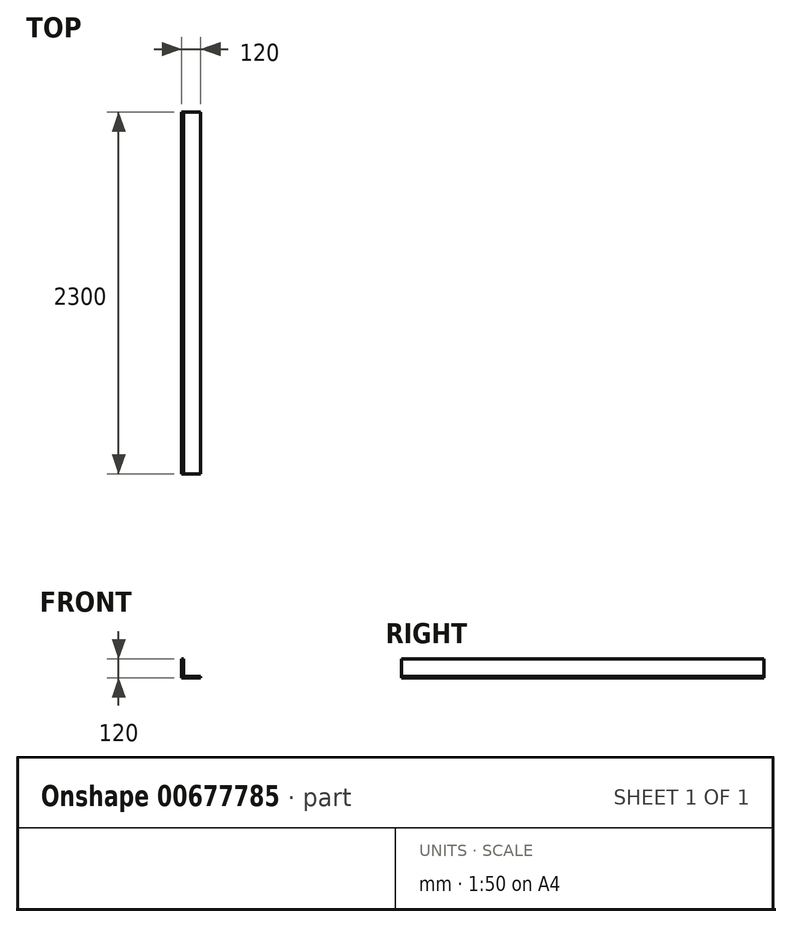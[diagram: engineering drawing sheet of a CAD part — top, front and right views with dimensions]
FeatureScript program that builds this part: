
annotation { "Feature Type Name" : "Feature", "Feature Type Description" : "" }
export const myFeature = defineFeature(function(context is Context, id is Id, definition is map)
    precondition{}
    {
        {
            var Q0;
            Q0=qCreatedBy(makeId("Front.planeOp"),FACE);
            var sketch = newSketch(context, id + "F0", { "sketchPlane" : qUnion([Q0])});
            skLineSegment(sketch, "E0.bottom", {"start": v(-43.33, -43.33) * mm, "end": v(76.67, -43.33) * mm});
            skLineSegment(sketch, "E0.top", {"start": v(-43.33, 76.67) * mm, "end": v(-33.33, 76.67) * mm});
            skLineSegment(sketch, "E0.left", {"start": v(-43.33, -43.33) * mm, "end": v(-43.33, 76.67) * mm});
            skLineSegment(sketch, "E0.right", {"start": v(76.67, -43.33) * mm, "end": v(76.67, -33.33) * mm});
            skLineSegment(sketch, "E1.0", {"start": v(-33.33, -33.33) * mm, "end": v(-33.33, 76.67) * mm});
            skLineSegment(sketch, "E1.1", {"start": v(-33.33, -33.33) * mm, "end": v(76.67, -33.33) * mm});
            skSolve(sketch);
        }
        {
            var Q0;
            Q0=makeQuery(id+"F0.imprint","IMPRINT",FACE,{"disambiguationData":[TD([[makeQuery(id+"F0.imprint","IMPRINT",EDGE,{"derivedFrom":sQuery(id+"F0.wireOp",EDGE,"E0.bottom")}),1.0]])]});
            extrude(context, id + "F1", {"entities" : qUnion([Q0]), "depth" : 2300 * mm, "offsetDistance" : 25 * mm});
        }
    });
